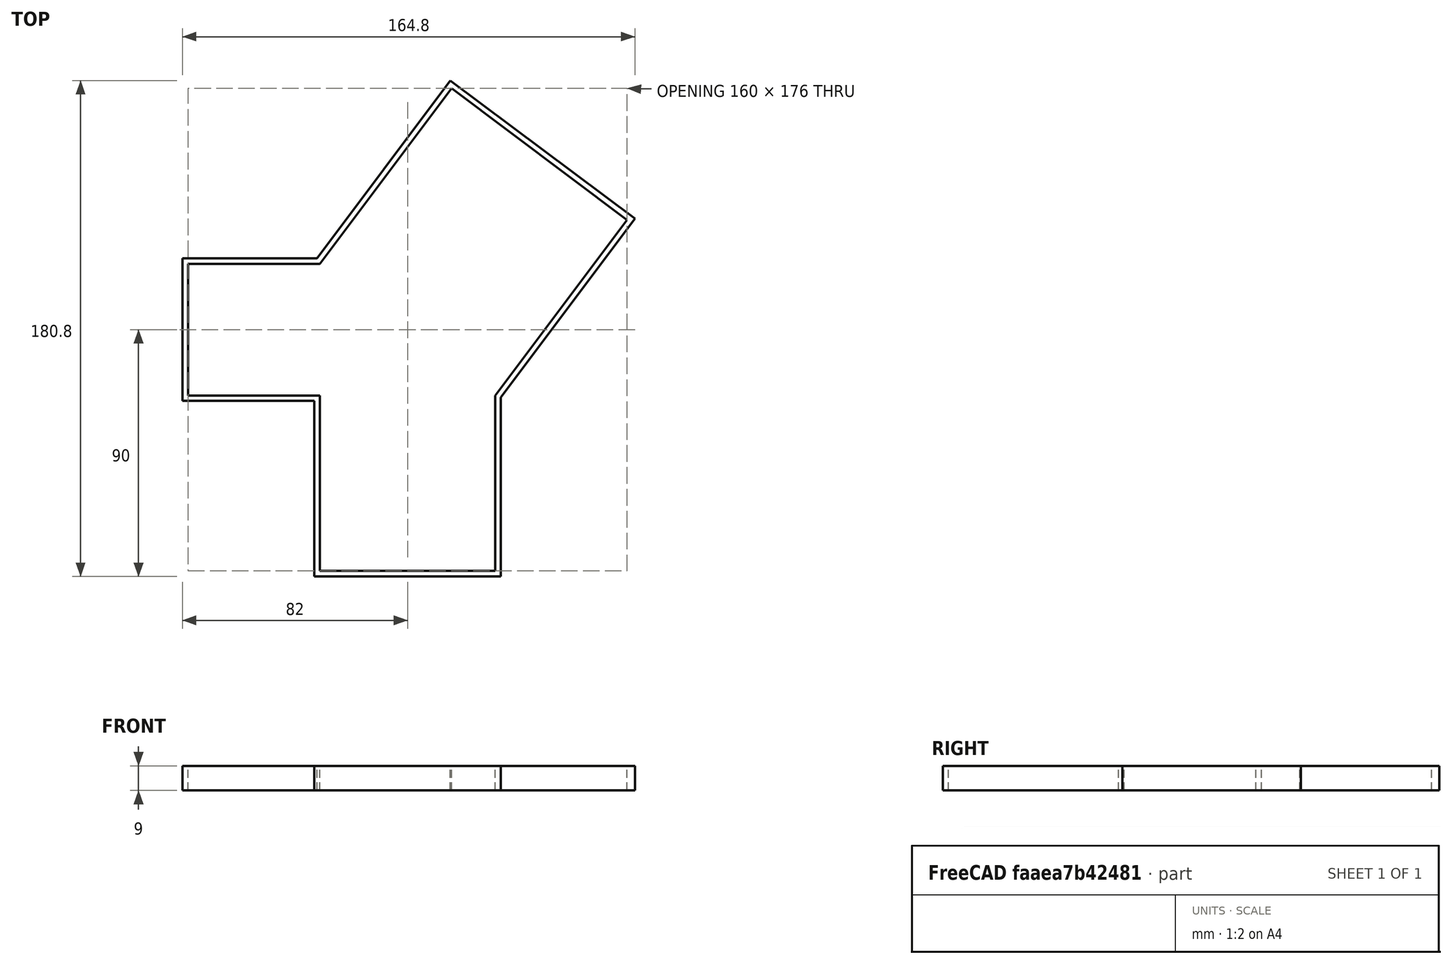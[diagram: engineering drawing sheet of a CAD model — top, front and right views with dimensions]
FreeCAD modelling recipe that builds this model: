
FCSTD DOCUMENT  (FreeCAD 0.17R13509 (Git))
Label: Teorema_Pitagoras
License: CreativeCommons Attribution-ShareAlike
LicenseURL: http://creativecommons.org/licenses/by-sa/4.0/
objects: Sketcher::SketchObject×1, PartDesign::Pad×1, PartDesign::Body×1
note: 4 computed .brp shape members not serialized (recipe doc carries the construction recipe); baked Part::Feature solids carry a one-line shape summary decoded from their .brp

FEATURE [Sketcher::SketchObject] Sketch
  MapMode = 5
  Support = -> [XY_Plane]
  sketch-geometry (19):
    g0: LineSegment StartX=0 StartY=48 StartZ=0 EndX=48 EndY=112 EndZ=0
    g1: LineSegment StartX=48 StartY=112 StartZ=0 EndX=112 EndY=64 EndZ=0
    g2: LineSegment StartX=112 StartY=64 StartZ=0 EndX=64 EndY=0 EndZ=0
    g3: LineSegment StartX=0 StartY=48 StartZ=0 EndX=-48 EndY=48 EndZ=0
    g4: LineSegment StartX=-48 StartY=48 StartZ=0 EndX=-48 EndY=0 EndZ=0
    g5: LineSegment StartX=-48 StartY=0 StartZ=0 EndX=0 EndY=0 EndZ=0
    g6: LineSegment StartX=64 StartY=0 StartZ=0 EndX=64 EndY=-64 EndZ=0
    g7: LineSegment StartX=64 StartY=-64 StartZ=0 EndX=0 EndY=-64 EndZ=0
    g8: LineSegment StartX=0 StartY=-64 StartZ=0 EndX=0 EndY=0 EndZ=0
    g9: LineSegment StartX=-1 StartY=50 StartZ=0 EndX=-50 EndY=50 EndZ=0
    g10: LineSegment StartX=-50 StartY=50 StartZ=0 EndX=-50 EndY=-2 EndZ=0
    g11: LineSegment StartX=-50 StartY=-2 StartZ=0 EndX=-2 EndY=-2 EndZ=0
    g12: LineSegment StartX=-2 StartY=-2 StartZ=0 EndX=-2 EndY=-66 EndZ=0
    g13: LineSegment StartX=-2 StartY=-66 StartZ=0 EndX=66 EndY=-66 EndZ=0
    g14: LineSegment StartX=66 StartY=-66 StartZ=0 EndX=66 EndY=-0.666667 EndZ=0
    g15: LineSegment StartX=66 StartY=-0.666667 StartZ=0 EndX=114.8 EndY=64.4 EndZ=0
    g16: LineSegment StartX=114.8 StartY=64.4 StartZ=0 EndX=47.6 EndY=114.8 EndZ=0
    g17: LineSegment StartX=-1 StartY=50 StartZ=0 EndX=47.6 EndY=114.8 EndZ=0
    g18: LineSegment [constr] StartX=0 StartY=48 StartZ=0 EndX=64 EndY=0 EndZ=0
  constraints (55):
    c: Coincident(g1,g2)
    c: Horizontal(g3)
    c: Coincident(g3,g4)
    c: PointOnObject(g4,g-1)
    c: Vertical(g4)
    c: Coincident(g4,g5)
    c: Coincident(g5,g-1)
    c: Vertical(g6)
    c: Coincident(g6,g7)
    c: Coincident(g7,g8)
    c: Coincident(g8,g-1)
    c: Vertical(g8)
    c: Parallel(g0,g2)
    c: Perpendicular(g1,g0)
    c: Horizontal(g7)
    c: Horizontal(g9)
    c: Coincident(g9,g10)
    c: Vertical(g10)
    c: Coincident(g10,g11)
    c: Horizontal(g11)
    c: Coincident(g11,g12)
    c: Vertical(g12)
    c: Coincident(g12,g13)
    c: Horizontal(g13)
    c: Coincident(g13,g14)
    c: Vertical(g14)
    c: Coincident(g14,g15)
    c: Coincident(g15,g16)
    c: DistanceX(g9,g3) = 2
    c: DistanceY(g11,g-1) = 2
    c: DistanceX(g11,g-1) = 2
    c: DistanceY(g12,g7) = 2
    c: DistanceX(g6,g13) = 2
    c: Coincident(g17,g16)
    c: DistanceY(g3,g9) = 2
    c: Distance(g9,g0) = 2
    c: Coincident(g17,g9)
    c: Parallel(g17,g0)
    c: Parallel(g2,g15)
    c: Coincident(g0,g1)
    c: Distance(g15,g2) = 2
    c: Distance(g16,g1) = 2
    c: Parallel(g16,g1)
    c: DistanceY(g-1,g0) = 48
    c: DistanceX(g-1,g2) = 64
    c: Coincident(g0,g3)
    c: PointOnObject(g0,g-2)
    c: Coincident(g2,g6)
    c: PointOnObject(g2,g-1)
    c: Equal(g4,g3)
    c: Equal(g0,g1)
    c: Equal(g6,g7)
    c: Coincident(g18,g0)
    c: Coincident(g18,g2)
    c: Parallel(g18,g1)
FEATURE [PartDesign::Pad] Pad
  Length = 9
  Length2 = 100
  Profile = -> Sketch
  Refine = true
  Type = 0
FEATURE [PartDesign::Body] Body
  Group = -> [Sketch,Pad]
  Origin = -> Origin
  Tip = -> Pad
